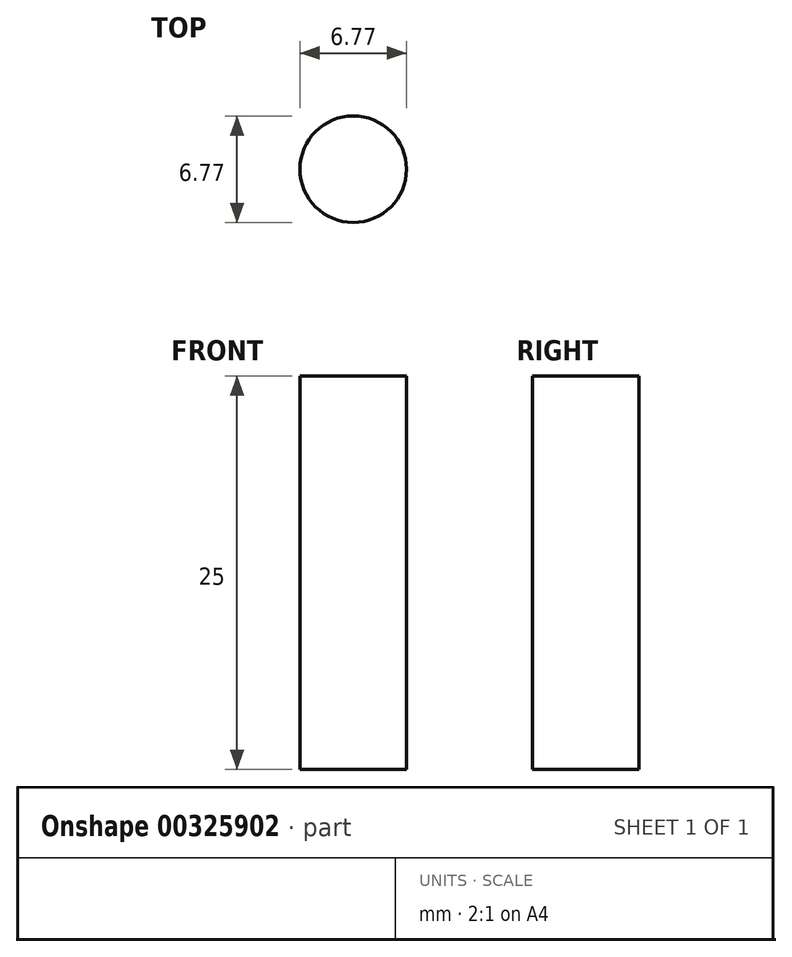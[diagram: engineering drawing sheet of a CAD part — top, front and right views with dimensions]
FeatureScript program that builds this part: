
annotation { "Feature Type Name" : "Feature", "Feature Type Description" : "" }
export const myFeature = defineFeature(function(context is Context, id is Id, definition is map)
    precondition{}
    {
        {
            var Q0;
            Q0=qCreatedBy(makeId("Top.planeOp"),FACE);
            var sketch = newSketch(context, id + "F0", { "sketchPlane" : qUnion([Q0])});
            skCircle(sketch, "E0", {"center": v(0, 0) * mm, "radius": 14.28 * mm});
            skCircle(sketch, "E1", {"center": v(17.87, 33.99) * mm, "radius": 3.38 * mm});
            skCircle(sketch, "E2", {"center": v(-22.08, 47.08) * mm, "radius": 8.3 * mm});
            skCircle(sketch, "E3", {"center": v(-13.95, 48.74) * mm, "radius": 1.6 * mm});
            skSolve(sketch);
        }
        {
            var Q0;
            Q0=makeQuery(id+"F0.imprint","IMPRINT",FACE,{"disambiguationData":[TD([[makeQuery(id+"F0.imprint","IMPRINT",EDGE,{"derivedFrom":sQuery(id+"F0.wireOp",EDGE,"E1")}),1.0]])]});
            extrude(context, id + "F1", {"entities" : qUnion([Q0]), "depth" : 25 * mm});
        }
    });
